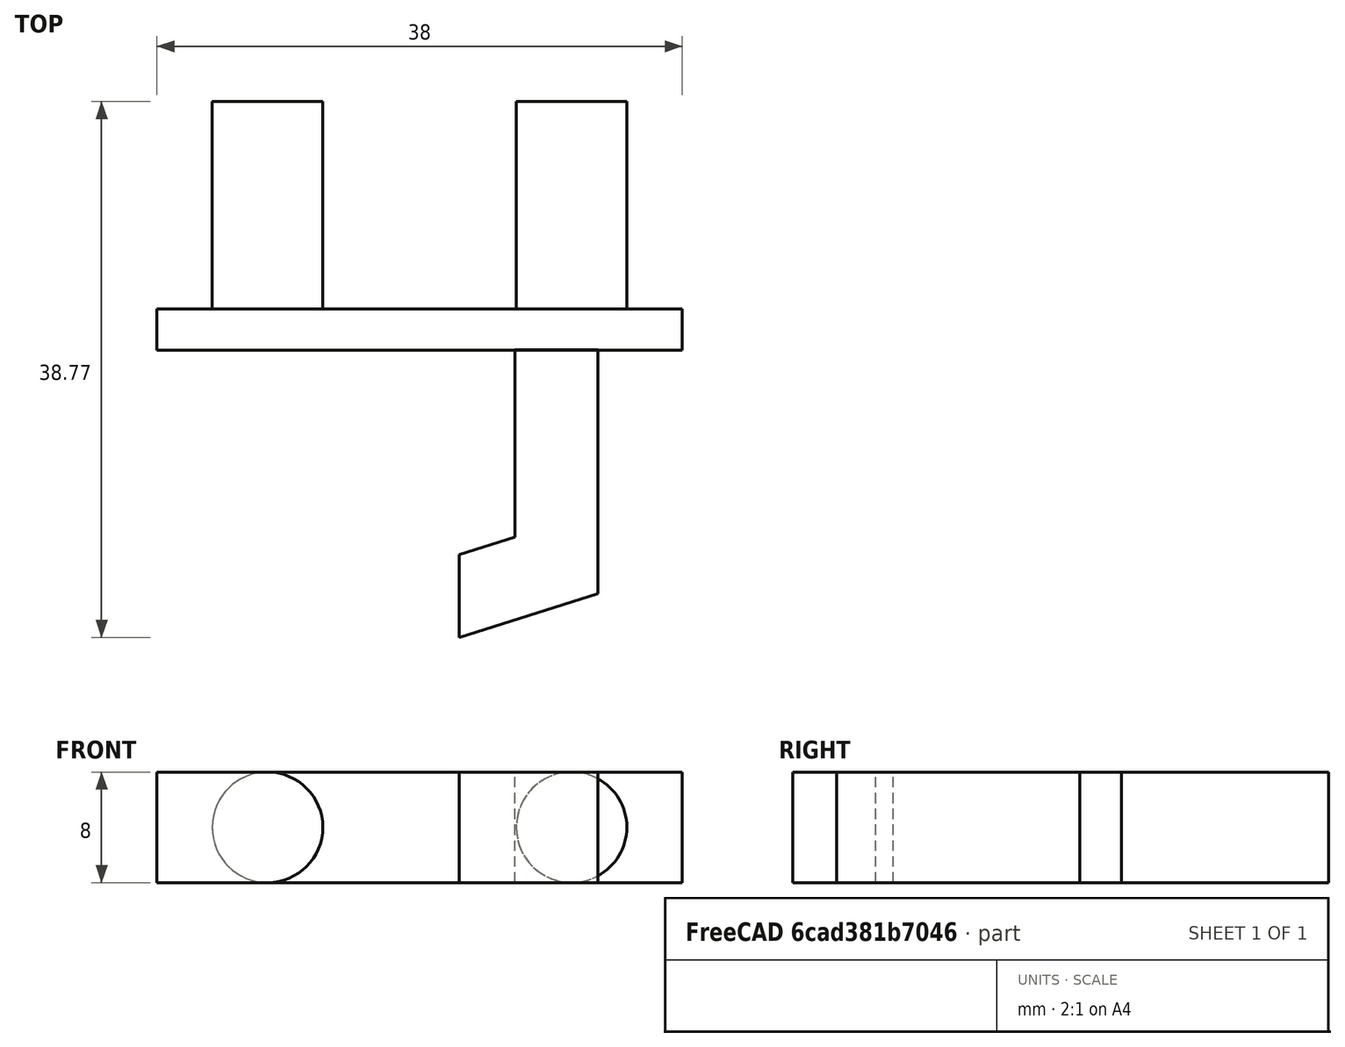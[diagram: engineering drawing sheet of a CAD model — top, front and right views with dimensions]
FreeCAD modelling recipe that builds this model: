
FCSTD DOCUMENT  (FreeCAD 0.15R4671 (Git))
Label: Hooks_V1
License: All rights reserved
LicenseURL: http://en.wikipedia.org/wiki/All_rights_reserved
objects: Part::Cylinder×2, Part::Box×1, Sketcher::SketchObject×1, PartDesign::Pad×1
note: 6 computed .brp shape members not serialized (recipe doc carries the construction recipe); baked Part::Feature solids carry a one-line shape summary decoded from their .brp

FEATURE [Part::Cylinder] Cylinder  label="Pin1"
  Angle = 360
  Height = 15
  Placement = pos=(0,0,0) rot=(1,0,0;1.5708rad)
  Radius = 4
FEATURE [Part::Cylinder] Cylinder001  label="Pin2"
  Angle = 360
  Height = 15
  Placement = pos=(22,0,0) rot=(1,0,0;1.5708rad)
  Radius = 4
FEATURE [Part::Box] Box  label="Base"
  Height = 8
  Length = 38
  Placement = pos=(-8,-18,-4) rot=(0,0,1;0rad)
  Width = 3
FEATURE [Sketcher::SketchObject] Sketch
  sketch-geometry (6):
    g0: LineSegment StartX=17.896 StartY=-17.9684 StartZ=0 EndX=23.896 EndY=-17.9684 EndZ=0
    g1: LineSegment StartX=23.896 StartY=-17.9684 StartZ=0 EndX=23.896 EndY=-35.5993 EndZ=0
    g2: LineSegment StartX=23.896 StartY=-35.5993 StartZ=0 EndX=13.8703 EndY=-38.7725 EndZ=0
    g3: LineSegment StartX=13.8703 StartY=-38.7725 StartZ=0 EndX=13.8703 EndY=-32.7725 EndZ=0
    g4: LineSegment StartX=13.8703 StartY=-32.7725 StartZ=0 EndX=17.896 EndY=-31.4984 EndZ=0
    g5: LineSegment StartX=17.896 StartY=-31.4984 StartZ=0 EndX=17.896 EndY=-17.9684 EndZ=0
  constraints (12):
    c: Coincident(g0,g1)
    c: Coincident(g1,g2)
    c: Coincident(g2,g3)
    c: Coincident(g3,g4)
    c: Coincident(g4,g5)
    c: Coincident(g5,g0)
    c: Distance(g0) = 6
    c: Distance(g3) = 6
    c: Parallel(g3,g-2)
    c: Parallel(g-2,g5)
    c: Parallel(g5,g1)
    c: Parallel(g4,g2)
FEATURE [PartDesign::Pad] Pad
  Length = 8
  Length2 = 100
  Midplane = true
  Sketch = -> Sketch
  Type = 0
